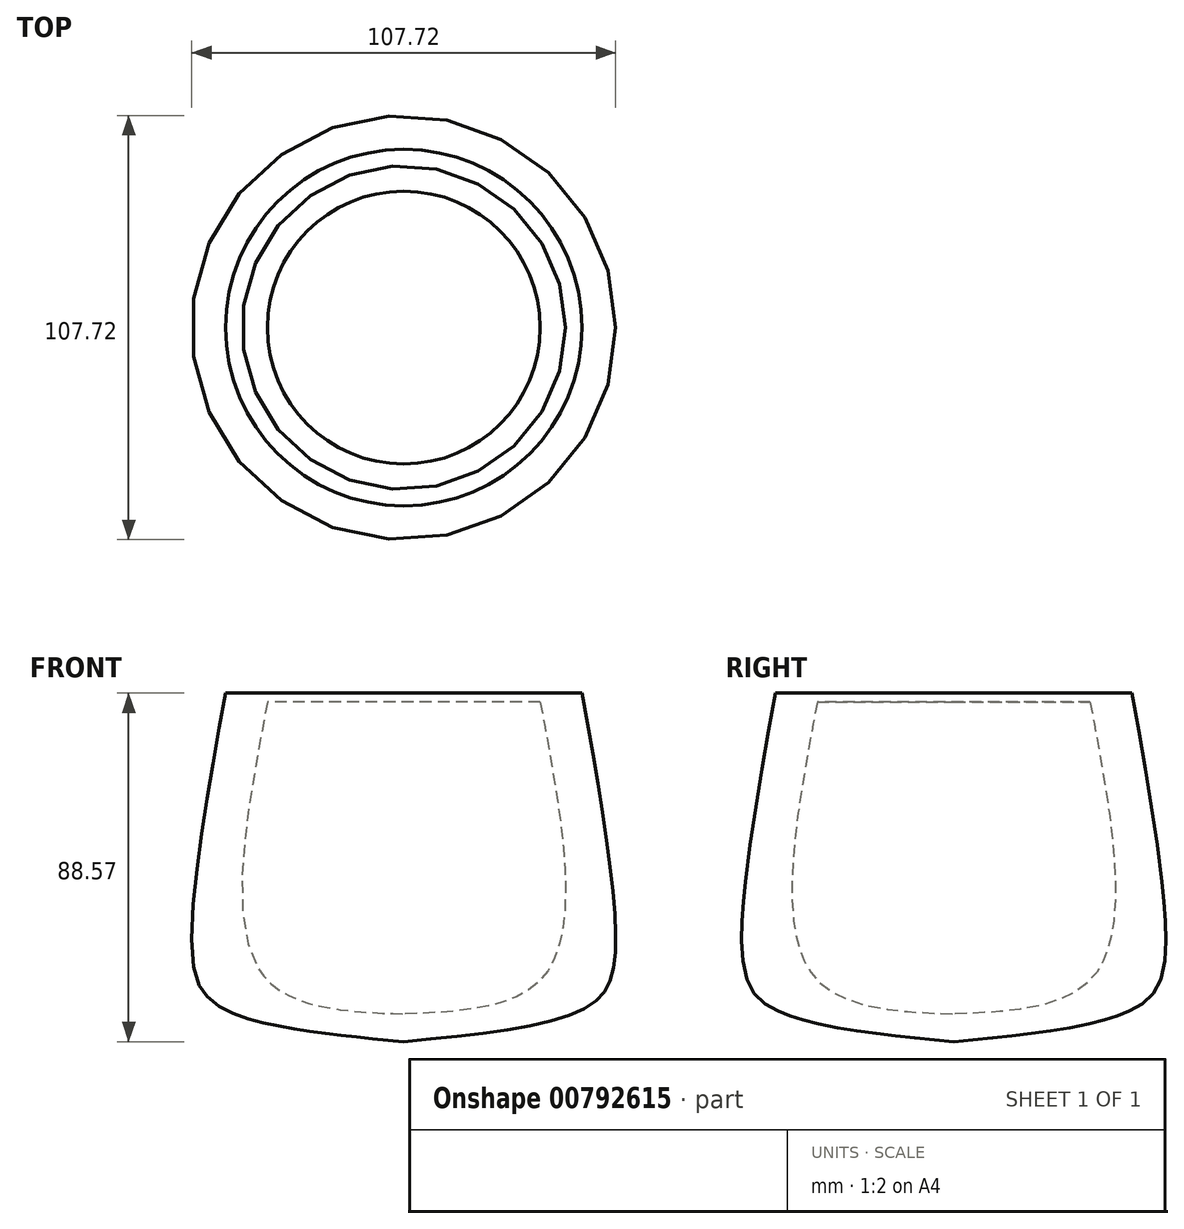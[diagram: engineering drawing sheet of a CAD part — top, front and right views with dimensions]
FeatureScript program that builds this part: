
annotation { "Feature Type Name" : "Feature", "Feature Type Description" : "" }
export const myFeature = defineFeature(function(context is Context, id is Id, definition is map)
    precondition{}
    {
        {
            var Q0;
            Q0=qCreatedBy(makeId("Front.planeOp"),FACE);
            var sketch = newSketch(context, id + "F0", { "sketchPlane" : qUnion([Q0])});
            skFitSpline(sketch, "E0", {"points": [v(34.66, 41.63) * mm, v(36.13, -27.3) * mm, v(0, -37.65) * mm], "startDerivative": vector(27.76, -147.3) * mm, "endDerivative": vector(-103.67, -4.07) * mm});
            skFitSpline(sketch, "E1", {"points": [v(45.28, 43.9) * mm, v(53.81, -21.16) * mm, v(47, -35.64) * mm, v(0, -44.67) * mm], "startDerivative": vector(32, -178.93) * mm, "endDerivative": vector(-158, -15) * mm});
            skLineSegment(sketch, "E2", {"start": v(0, 0) * mm, "end": v(0, 58.32) * mm});
            skLineSegment(sketch, "E3", {"start": v(0, 0) * mm, "end": v(0, -44.67) * mm});
            skSolve(sketch);
        }
        {
            var Q0;
            Q0=sQuery(id+"F0.wireOp",EDGE,"E0");
            var Q1;
            Q1=sQuery(id+"F0.wireOp",EDGE,"E1");
            var Q2;
            Q2=sQuery(id+"F0.wireOp",EDGE,"E2");
            revolve(context, id + "F1", {"bodyType" : ToolBodyType.SURFACE, "surfaceOperationType" : NewSurfaceOperationType.NEW, "surfaceEntities" : qUnion([Q0, Q1]), "axis" : qUnion([Q2]), "revolveType" : RevolveType.FULL});
        }
    });
